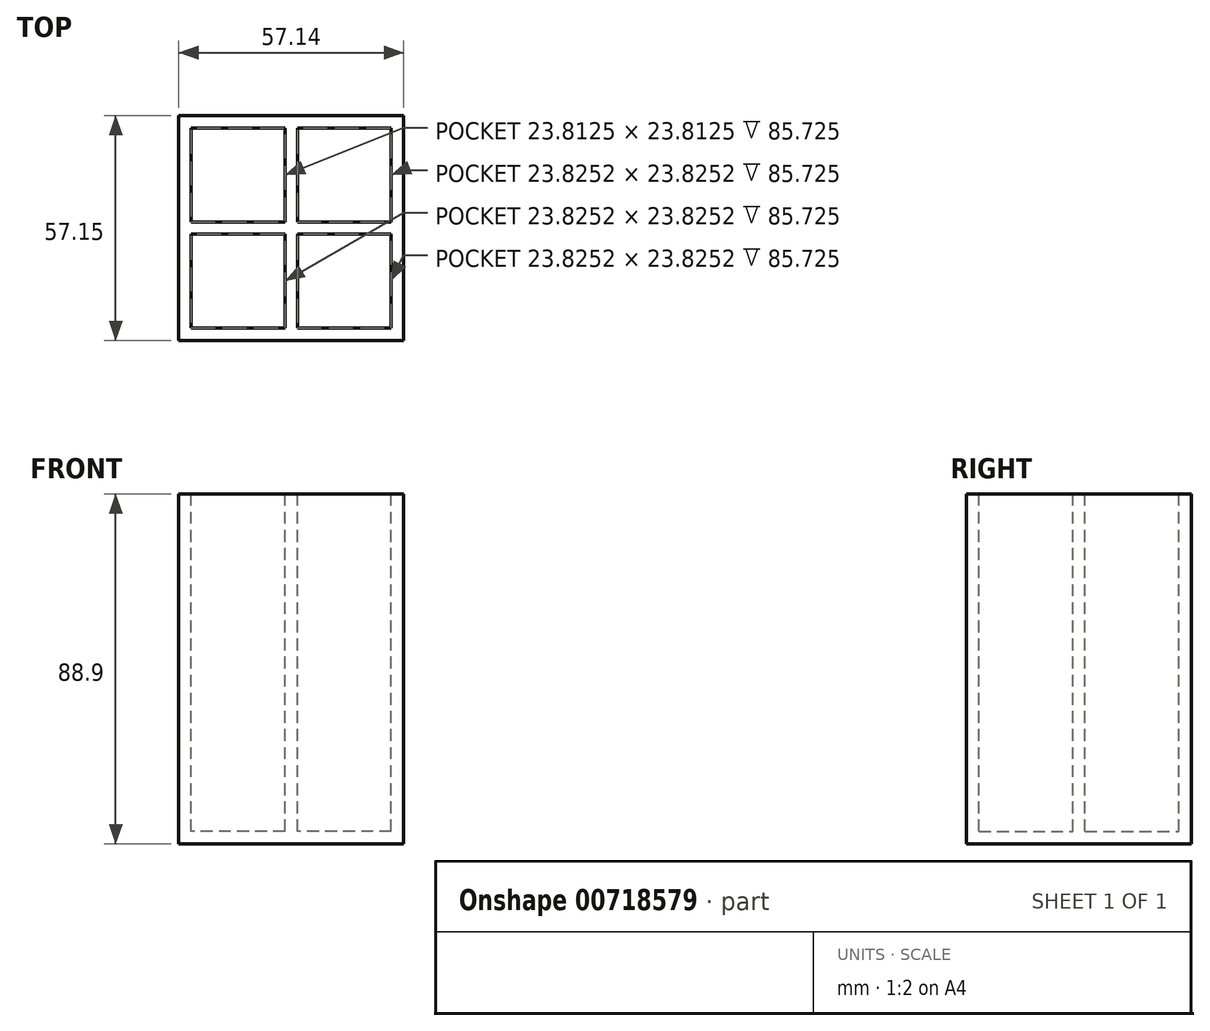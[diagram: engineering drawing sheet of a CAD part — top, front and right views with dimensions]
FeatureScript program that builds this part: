
annotation { "Feature Type Name" : "Feature", "Feature Type Description" : "" }
export const myFeature = defineFeature(function(context is Context, id is Id, definition is map)
    precondition{}
    {
        {
            var Q0;
            Q0=qCreatedBy(makeId("Front.planeOp"),FACE);
            var sketch = newSketch(context, id + "F0", { "sketchPlane" : qUnion([Q0])});
            skLineSegment(sketch, "E0.bottom", {"start": v(-28.58, 44.45) * mm, "end": v(28.58, 44.45) * mm});
            skLineSegment(sketch, "E0.top", {"start": v(-28.58, -44.45) * mm, "end": v(28.58, -44.45) * mm});
            skLineSegment(sketch, "E0.left", {"start": v(-28.58, 44.45) * mm, "end": v(-28.57, -44.45) * mm});
            skLineSegment(sketch, "E0.right", {"start": v(28.58, 44.45) * mm, "end": v(28.58, -44.45) * mm});
            skPoint(sketch, "E0.middle", {"position": v(0, 0) * mm});
            skSolve(sketch);
        }
        {
            var Q0;
            Q0 = qSketchRegion(id + "F0", true);
            extrude(context, id + "F1", {"entities" : qUnion([Q0]), "depth" : 57.15 * mm, "offsetDistance" : 25.4 * mm});
        }
        {
            var Q0;
            Q0=makeQuery(id+"F1.opExtrude","SWEPT_FACE",FACE,{"disambiguationData":[OSD([sQuery(id+"F0.wireOp",EDGE,"E0.bottom")])]});
            var sketch = newSketch(context, id + "F2", { "sketchPlane" : qUnion([Q0])});
            skLineSegment(sketch, "E1.bottom", {"start": v(-1.59, -26.99) * mm, "end": v(-25.4, -26.99) * mm});
            skLineSegment(sketch, "E1.top", {"start": v(-1.59, -3.17) * mm, "end": v(-25.4, -3.18) * mm});
            skLineSegment(sketch, "E1.left", {"start": v(-1.59, -26.99) * mm, "end": v(-1.59, -3.17) * mm});
            skLineSegment(sketch, "E1.right", {"start": v(-25.4, -26.99) * mm, "end": v(-25.4, -3.17) * mm});
            skPoint(sketch, "E1.middle", {"position": v(-13.5, -15.08) * mm});
            skSolve(sketch);
        }
        {
            var Q0;
            Q0 = qSketchRegion(id + "F2", true);
            extrude(context, id + "F3", {"entities" : qUnion([Q0]), "operationType" : NewBodyOperationType.REMOVE, "oppositeDirection" : true, "depth" : 85.72 * mm, "offsetDistance" : 25.4 * mm});
        }
        {
            var Q0;
            Q0=makeQuery(id+"F1.opExtrude","SWEPT_FACE",FACE,{"disambiguationData":[OSD([sQuery(id+"F0.wireOp",EDGE,"E0.bottom")])]});
            var sketch = newSketch(context, id + "F4", { "sketchPlane" : qUnion([Q0])});
            skLineSegment(sketch, "E2.bottom", {"start": v(25.4, -27) * mm, "end": v(1.57, -27) * mm});
            skLineSegment(sketch, "E2.top", {"start": v(25.4, -3.18) * mm, "end": v(1.57, -3.18) * mm});
            skLineSegment(sketch, "E2.left", {"start": v(25.4, -27) * mm, "end": v(25.4, -3.18) * mm});
            skLineSegment(sketch, "E2.right", {"start": v(1.57, -27) * mm, "end": v(1.57, -3.18) * mm});
            skPoint(sketch, "E2.middle", {"position": v(13.49, -15.09) * mm});
            skSolve(sketch);
        }
        {
            var Q0;
            Q0 = qSketchRegion(id + "F4", true);
            extrude(context, id + "F5", {"entities" : qUnion([Q0]), "operationType" : NewBodyOperationType.REMOVE, "oppositeDirection" : true, "depth" : 85.72 * mm, "offsetDistance" : 25.4 * mm});
        }
        {
            var Q0;
            Q0=makeQuery(id+"F1.opExtrude","SWEPT_FACE",FACE,{"disambiguationData":[OSD([sQuery(id+"F0.wireOp",EDGE,"E0.bottom")])]});
            var sketch = newSketch(context, id + "F6", { "sketchPlane" : qUnion([Q0])});
            skLineSegment(sketch, "E3.bottom", {"start": v(-1.57, -53.98) * mm, "end": v(-25.4, -53.98) * mm});
            skLineSegment(sketch, "E3.top", {"start": v(-1.57, -30.15) * mm, "end": v(-25.4, -30.15) * mm});
            skLineSegment(sketch, "E3.left", {"start": v(-1.57, -53.98) * mm, "end": v(-1.57, -30.15) * mm});
            skLineSegment(sketch, "E3.right", {"start": v(-25.4, -53.98) * mm, "end": v(-25.4, -30.15) * mm});
            skPoint(sketch, "E3.middle", {"position": v(-13.49, -42.06) * mm});
            skSolve(sketch);
        }
        {
            var Q0;
            Q0 = qSketchRegion(id + "F6", true);
            extrude(context, id + "F7", {"entities" : qUnion([Q0]), "operationType" : NewBodyOperationType.REMOVE, "oppositeDirection" : true, "depth" : 85.72 * mm, "offsetDistance" : 25.4 * mm});
        }
        {
            var Q0;
            Q0=makeQuery(id+"F1.opExtrude","SWEPT_FACE",FACE,{"disambiguationData":[OSD([sQuery(id+"F0.wireOp",EDGE,"E0.bottom")])]});
            var sketch = newSketch(context, id + "F8", { "sketchPlane" : qUnion([Q0])});
            skLineSegment(sketch, "E4.bottom", {"start": v(1.57, -30.15) * mm, "end": v(25.4, -30.15) * mm});
            skLineSegment(sketch, "E4.top", {"start": v(1.57, -53.98) * mm, "end": v(25.4, -53.98) * mm});
            skLineSegment(sketch, "E4.left", {"start": v(1.57, -30.15) * mm, "end": v(1.57, -53.98) * mm});
            skLineSegment(sketch, "E4.right", {"start": v(25.4, -30.15) * mm, "end": v(25.4, -53.98) * mm});
            skPoint(sketch, "E4.middle", {"position": v(13.49, -42.06) * mm});
            skSolve(sketch);
        }
        {
            var Q0;
            Q0 = qSketchRegion(id + "F8", true);
            extrude(context, id + "F9", {"entities" : qUnion([Q0]), "operationType" : NewBodyOperationType.REMOVE, "oppositeDirection" : true, "depth" : 85.72 * mm, "offsetDistance" : 25.4 * mm});
        }
    });
